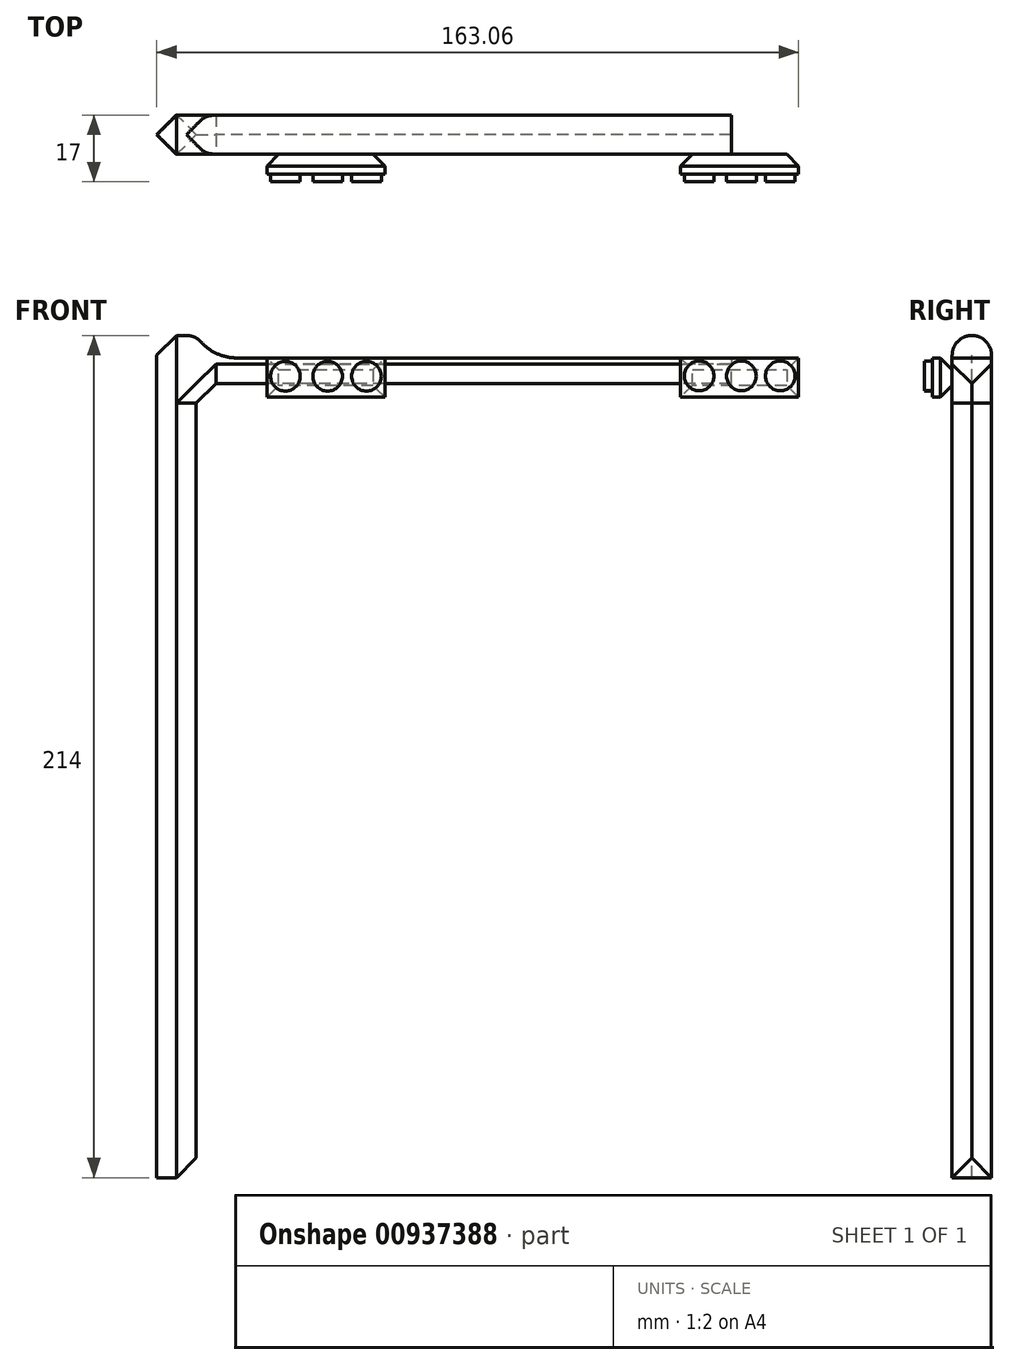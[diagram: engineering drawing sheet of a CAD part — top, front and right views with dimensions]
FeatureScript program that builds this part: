
annotation { "Feature Type Name" : "Feature", "Feature Type Description" : "" }
export const myFeature = defineFeature(function(context is Context, id is Id, definition is map)
    precondition{}
    {
        {
            var Q0;
            Q0=qCreatedBy(makeId("Top.planeOp"),FACE);
            var sketch = newSketch(context, id + "F0", { "sketchPlane" : qUnion([Q0])});
            skLineSegment(sketch, "E0.bottom", {"start": v(-5, 5) * mm, "end": v(5, 5) * mm});
            skLineSegment(sketch, "E0.top", {"start": v(-5, -5) * mm, "end": v(5, -5) * mm});
            skLineSegment(sketch, "E0.left", {"start": v(-5, 5) * mm, "end": v(-5, -5) * mm});
            skLineSegment(sketch, "E0.right", {"start": v(5, 5) * mm, "end": v(5, -5) * mm});
            skSolve(sketch);
        }
        {
            var Q0;
            Q0=makeQuery(id+"F0.imprint","IMPRINT",FACE,{"disambiguationData":[TD([[makeQuery(id+"F0.imprint","IMPRINT",EDGE,{"derivedFrom":sQuery(id+"F0.wireOp",EDGE,"E0.bottom")}),-1.0]])]});
            extrude(context, id + "F1", {"entities" : qUnion([Q0]), "depth" : 214 * mm, "offsetDistance" : 25 * mm});
        }
        {
            var Q0;
            Q0=makeQuery(id+"F1.opExtrude","SWEPT_FACE",FACE,{"disambiguationData":[OSD([sQuery(id+"F0.wireOp",EDGE,"E0.right")])]});
            var sketch = newSketch(context, id + "F2", { "sketchPlane" : qUnion([Q0])});
            skLineSegment(sketch, "E1.bottom", {"start": v(-5, 208.28) * mm, "end": v(5, 208.28) * mm});
            skLineSegment(sketch, "E1.top", {"start": v(-5, 201.75) * mm, "end": v(5, 201.75) * mm});
            skLineSegment(sketch, "E1.left", {"start": v(-5, 208.28) * mm, "end": v(-5, 201.75) * mm});
            skLineSegment(sketch, "E1.right", {"start": v(5, 208.28) * mm, "end": v(5, 201.75) * mm});
            skSolve(sketch);
        }
        {
            var Q0;
            Q0=makeQuery(id+"F2.imprint","IMPRINT",FACE,{"disambiguationData":[TD([[makeQuery(id+"F2.imprint","IMPRINT",EDGE,{"derivedFrom":sQuery(id+"F2.wireOp",EDGE,"E1.bottom")}),-1.0]])]});
            extrude(context, id + "F3", {"entities" : qUnion([Q0]), "operationType" : NewBodyOperationType.ADD, "depth" : 136 * mm, "offsetDistance" : 25 * mm});
        }
        {
            var Q0;
            Q0=makeQuery(id+"F3.opExtrude","CAP_EDGE",EDGE,{"disambiguationData":[OSD([sQuery(id+"F2.wireOp",EDGE,"E1.bottom")])],"isStart":true});
            var Q1;
            Q1=makeQuery(id+"F3.opExtrude","CAP_EDGE",EDGE,{"disambiguationData":[OSD([sQuery(id+"F2.wireOp",EDGE,"E1.top")])],"isStart":true});
            fillet(context, id + "F4", {"entities" : qUnion([Q0, Q1]), "radius" : 12.07 * mm, "tangentPropagation" : true, "allowEdgeOverflow" : false});
        }
        {
            var Q0;
            Q0=makeQuery(id+"F1.opExtrude","CAP_FACE",FACE,{"disambiguationData":[OSD([sQuery(id+"F0.wireOp",EDGE,"E0.bottom"),sQuery(id+"F0.wireOp",EDGE,"E0.top"),sQuery(id+"F0.wireOp",EDGE,"E0.left"),sQuery(id+"F0.wireOp",EDGE,"E0.right")])],"isStart":false});
            fillet(context, id + "F5", {"entities" : qUnion([Q0]), "radius" : 5 * mm, "tangentPropagation" : true, "allowEdgeOverflow" : false});
        }
        {
            var Q0;
            Q0=makeQuery(id+"F3.boolean.opBoolean","MERGE",FACE,{"derivedFrom":[makeQuery(id+"F1.opExtrude","SWEPT_FACE",FACE,{"disambiguationData":[OSD([sQuery(id+"F0.wireOp",EDGE,"E0.top")])]}),makeQuery(id+"F3.opExtrude","SWEPT_FACE",FACE,{"disambiguationData":[OSD([sQuery(id+"F2.wireOp",EDGE,"E1.left")])]})]});
            var sketch = newSketch(context, id + "F6", { "sketchPlane" : qUnion([Q0])});
            skLineSegment(sketch, "E2.bottom", {"start": v(22.98, 208.28) * mm, "end": v(52.98, 208.28) * mm});
            skLineSegment(sketch, "E2.top", {"start": v(22.98, 198.28) * mm, "end": v(52.98, 198.28) * mm});
            skLineSegment(sketch, "E2.left", {"start": v(22.98, 208.28) * mm, "end": v(22.98, 198.28) * mm});
            skLineSegment(sketch, "E2.right", {"start": v(52.98, 208.28) * mm, "end": v(52.98, 198.28) * mm});
            skLineSegment(sketch, "E3.bottom", {"start": v(128.06, 208.28) * mm, "end": v(158.06, 208.28) * mm});
            skLineSegment(sketch, "E3.top", {"start": v(128.06, 198.28) * mm, "end": v(158.06, 198.28) * mm});
            skLineSegment(sketch, "E3.left", {"start": v(128.06, 208.28) * mm, "end": v(128.06, 198.28) * mm});
            skLineSegment(sketch, "E3.right", {"start": v(158.06, 208.28) * mm, "end": v(158.06, 198.28) * mm});
            skSolve(sketch);
        }
        {
            var Q0;
            {var subQ0=sQuery(id+"F6.wireOp",EDGE,"E2.bottom");Q0=makeQuery(id+"F6.imprint","IMPRINT",FACE,{"disambiguationData":[TD([[makeQuery(id+"F6.imprint","IMPRINT",EDGE,{"derivedFrom":subQ0}),1.0]])]});}
            var Q1;
            {var subQ0=sQuery(id+"F6.wireOp",EDGE,"E2.top");Q1=makeQuery(id+"F6.imprint","IMPRINT",FACE,{"disambiguationData":[TD([[makeQuery(id+"F6.imprint","IMPRINT",EDGE,{"derivedFrom":subQ0}),1.0]])]});}
            var Q2;
            {var subQ6=sQuery(id+"F6.wireOp",EDGE,"E3.top");Q2=makeQuery(id+"F6.imprint","IMPRINT",FACE,{"disambiguationData":[TD([[makeQuery(id+"F6.imprint","IMPRINT",EDGE,{"derivedFrom":subQ6}),1.0]])]});}
            var Q3;
            {var subQ1=sQuery(id+"F2.wireOp",EDGE,"E1.left");var subQ2=makeQuery(id+"F3.opExtrude","CAP_EDGE",EDGE,{"disambiguationData":[OSD([subQ1])],"isStart":false});Q3=makeQuery(id+"F6.imprint","IMPRINT",FACE,{"disambiguationData":[TD([[makeQuery(id+"F6.imprint","IMPRINT",EDGE,{"derivedFrom":subQ2}),-1.0]])]});}
            extrude(context, id + "F7", {"entities" : qUnion([Q0, Q1, Q2, Q3]), "depth" : 5 * mm, "offsetDistance" : 25 * mm});
        }
        {
            var Q0;
            Q0=makeQuery(id+"F7.opExtrude","CAP_FACE",FACE,{"disambiguationData":[OSD([sQuery(id+"F6.wireOp",EDGE,"E3.bottom"),sQuery(id+"F6.wireOp",EDGE,"E3.top"),sQuery(id+"F6.wireOp",EDGE,"E3.left"),sQuery(id+"F6.wireOp",EDGE,"E3.right")])],"isStart":true});
            var Q1;
            Q1=makeQuery(id+"F7.opExtrude","CAP_FACE",FACE,{"disambiguationData":[OSD([sQuery(id+"F6.wireOp",EDGE,"E2.bottom"),sQuery(id+"F6.wireOp",EDGE,"E2.top"),sQuery(id+"F6.wireOp",EDGE,"E2.left"),sQuery(id+"F6.wireOp",EDGE,"E2.right")])],"isStart":true});
            chamfer(context, id + "F8", {"entities" : qUnion([Q0, Q1]), "width" : 3 * mm, "tangentPropagation" : true});
        }
        {
            var Q0;
            Q0=makeQuery(id+"F7.opExtrude","CAP_FACE",FACE,{"disambiguationData":[OSD([sQuery(id+"F6.wireOp",EDGE,"E2.bottom"),sQuery(id+"F6.wireOp",EDGE,"E2.top"),sQuery(id+"F6.wireOp",EDGE,"E2.left"),sQuery(id+"F6.wireOp",EDGE,"E2.right")])],"isStart":false});
            var sketch = newSketch(context, id + "F9", { "sketchPlane" : qUnion([Q0])});
            skCircle(sketch, "E4", {"center": v(27.65, 203.6) * mm, "radius": 3.77 * mm});
            skCircle(sketch, "E5", {"center": v(38.39, 203.6) * mm, "radius": 3.77 * mm});
            skCircle(sketch, "E6", {"center": v(48.25, 203.6) * mm, "radius": 3.77 * mm});
            skSolve(sketch);
        }
        {
            var Q0;
            Q0=makeQuery(id+"F9.imprint","IMPRINT",FACE,{"disambiguationData":[TD([[makeQuery(id+"F9.imprint","IMPRINT",EDGE,{"derivedFrom":sQuery(id+"F9.wireOp",EDGE,"E4")}),1.0]])]});
            var Q1;
            Q1=makeQuery(id+"F9.imprint","IMPRINT",FACE,{"disambiguationData":[TD([[makeQuery(id+"F9.imprint","IMPRINT",EDGE,{"derivedFrom":sQuery(id+"F9.wireOp",EDGE,"E5")}),1.0]])]});
            var Q2;
            Q2=makeQuery(id+"F9.imprint","IMPRINT",FACE,{"disambiguationData":[TD([[makeQuery(id+"F9.imprint","IMPRINT",EDGE,{"derivedFrom":sQuery(id+"F9.wireOp",EDGE,"E6")}),1.0]])]});
            extrude(context, id + "F10", {"entities" : qUnion([Q0, Q1, Q2]), "operationType" : NewBodyOperationType.ADD, "depth" : 2 * mm, "offsetDistance" : 25 * mm});
        }
        {
            var Q0;
            Q0=makeQuery(id+"F7.opExtrude","CAP_FACE",FACE,{"disambiguationData":[OSD([sQuery(id+"F6.wireOp",EDGE,"E3.bottom"),sQuery(id+"F6.wireOp",EDGE,"E3.top"),sQuery(id+"F6.wireOp",EDGE,"E3.left"),sQuery(id+"F6.wireOp",EDGE,"E3.right")])],"isStart":false});
            var sketch = newSketch(context, id + "F11", { "sketchPlane" : qUnion([Q0])});
            skCircle(sketch, "E7", {"center": v(132.78, 203.71) * mm, "radius": 3.77 * mm});
            skCircle(sketch, "E8", {"center": v(143.52, 203.71) * mm, "radius": 3.77 * mm});
            skCircle(sketch, "E9", {"center": v(153.38, 203.71) * mm, "radius": 3.77 * mm});
            skSolve(sketch);
        }
        {
            var Q0;
            Q0 = qSketchRegion(id + "F11", true);
            extrude(context, id + "F12", {"entities" : qUnion([Q0]), "operationType" : NewBodyOperationType.ADD, "depth" : 2 * mm, "offsetDistance" : 25 * mm});
        }
        {
            var Q0;
            Q0=makeQuery(id+"F1.opExtrude","SWEPT_EDGE",EDGE,{"disambiguationData":[OSD([sQuery(id+"F0.wireOp",EDGE,"E0.top"),sQuery(id+"F0.wireOp",EDGE,"E0.left")])]});
            var Q1;
            {var subQ1=sQuery(id+"F0.wireOp",EDGE,"E0.right");Q1=makeQuery(id+"F3.boolean.opBoolean","SPLIT",FACE,{"disambiguationData":[TD([makeQuery(id+"F3.opExtrude","SWEPT_FACE",FACE,{"disambiguationData":[OSD([sQuery(id+"F2.wireOp",EDGE,"E1.top")])]})])],"derivedFrom":makeQuery(id+"F1.opExtrude","SWEPT_FACE",FACE,{"disambiguationData":[OSD([subQ1])]})});}
            chamfer(context, id + "F13", {"entities" : qUnion([Q0, Q1]), "width" : 5 * mm, "tangentPropagation" : true});
        }
    });
